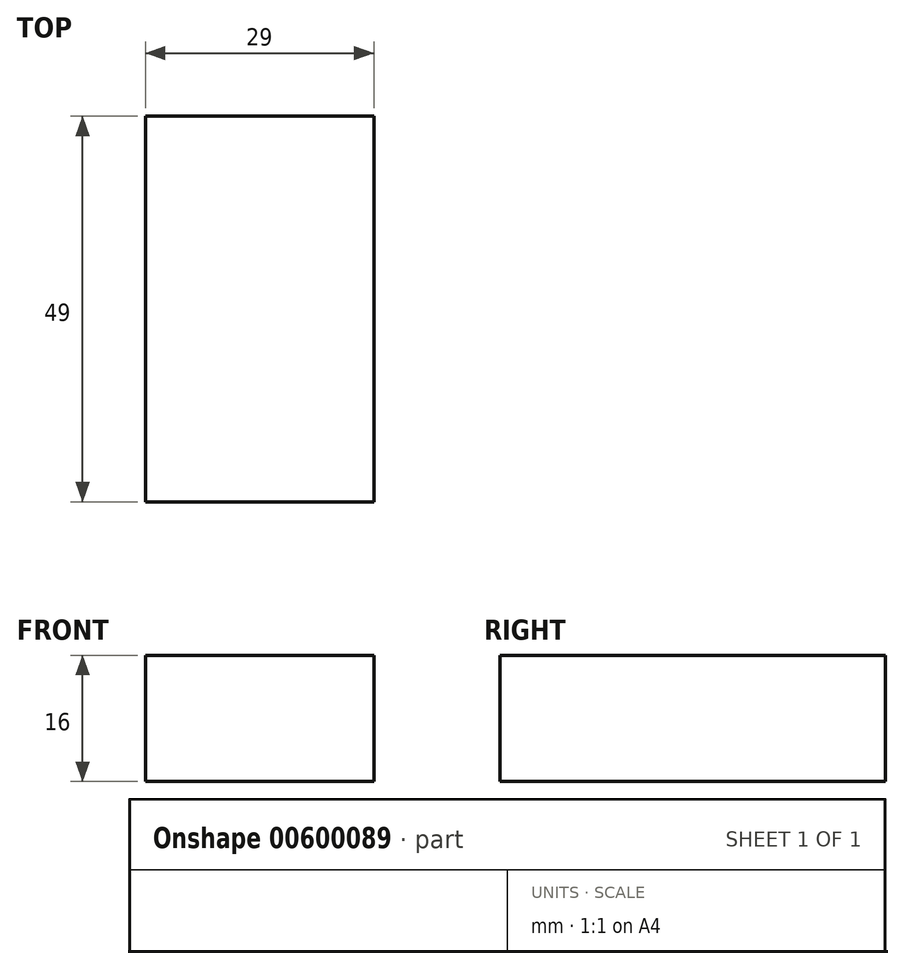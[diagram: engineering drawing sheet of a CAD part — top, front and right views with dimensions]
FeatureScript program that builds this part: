
annotation { "Feature Type Name" : "Feature", "Feature Type Description" : "" }
export const myFeature = defineFeature(function(context is Context, id is Id, definition is map)
    precondition{}
    {
        {
            var Q0;
            Q0=qCreatedBy(makeId("Top.planeOp"),FACE);
            var sketch = newSketch(context, id + "F0", { "sketchPlane" : qUnion([Q0])});
            skLineSegment(sketch, "E0.bottom", {"start": v(-14.5, 24.5) * mm, "end": v(14.5, 24.5) * mm});
            skLineSegment(sketch, "E0.top", {"start": v(-14.5, -24.5) * mm, "end": v(14.5, -24.5) * mm});
            skLineSegment(sketch, "E0.left", {"start": v(-14.5, 24.5) * mm, "end": v(-14.5, -24.5) * mm});
            skLineSegment(sketch, "E0.right", {"start": v(14.5, 24.5) * mm, "end": v(14.5, -24.5) * mm});
            skPoint(sketch, "E0.middle", {"position": v(0, 0) * mm});
            skSolve(sketch);
        }
        {
            var Q0;
            Q0=qSketchRegion(id+"F0",true);
            extrude(context, id + "F1", {"entities" : qUnion([Q0]), "depth" : 16 * mm});
        }
    });
